# Revit family: PRD_FrankeWS_WtrSpplFttngsFrWshBsnsAndTrghs_PillarMixer_F5EM1001-1004,1007-1010
name_source: partatom
category: Plumbing Fixtures
revit_build: Autodesk Revit 2018 (Build: 20190510_1515(x64)
units: mm (PartAtom-declared; Revit-internal decimal feet)

## family parameters
Always vertical = Yes
Cut with Voids When Loaded = No
OmniClass Number = 23.45.55.14
OmniClass Title = Single Faucets
Part Type = Normal
Room Calculation Point = No
Round Connector Dimension = Use Diameter
Shared = No
Work Plane-Based = No

## types (8) — shared parameters
AssetType = Fixed
Category = Pr_40_20_87_98, Washbasin taps
Color = Chrome
DefaultAutomaticHygieneFlushing = 24H-AFTER-ACTIVITY
Depressurised = no
DurationUnit = year
FaucetFunction = MIXED
FaucetMaterial = PRD_AR_ChromatedBrass_HighPolished
FaucetOperation = SELFCLOSING
FaucetType = PILLAR
Finish = high-polished chromium-plated brass
FlowColdWater = 0.1 L/s
FlowHotWater = 0.1 L/s
Form = Self-closing
FunctionalPrinciple = ELECTRONIX-C
HygieneFlushing = yes
IfcExportAs = IfcValveType
IfcExportType = FAUCET
InletSize = G 3/8
Manufacturer = KWC Group AG
ManufacturerName = KWC Group AG
ManufacturerURL = www.kwc.com
Material = Brass
MaterialsBody = Brass
MaterialsFinishAndColour = high-polished chromium-plated brass
MinimumFlowPressure = 1.00 bar
NBSDescription = Water supply fittings for wash basins and troughs
NBSReference = 45-35-70/371
OutletMaterial = PRD_AR_SyntheticGrey
ProductInformation = https://pim.kwc.com
ProtectiveShutdown = yes
ProtectiveSystemIP = 59K
SensorMaterial = PRD_AR_SyntheticDarkGrey
SoundInsulation = no
SpoutProjection = 125.00 mm
ThermalDisinfection = no
TypeOfMixing = yes
TypeOfMounting = TAPHOLE
TypeOfOperation = SENSOR-OPERATION
TypeOfSensor = OPTO-ELEC-SENSOR
TypeOfTap = PILLAR-TAP
URL = www.kwc.com
Uniclass2015Code = Pr_40_20_87_98
Uniclass2015Title = Washbasin taps
Uniclass2015Version = Products v1.7
Version = 1
WarrantyDurationUnit = year
zero-valued in all types: NominalHeight, NominalLength, NominalWidth

## per-type parameters (varying)
| type | BIMObjectName | Description | FlowRateMaximum | GrossWeight | Model | ModelNumber | ModelReference | Name | NetWeight | NominalDiameter | PositionOfPowerConnection | PowerConsumption | PowerSupplyConnection |
| F5EM1001 - 0.08 L/s with 6 V lithium battery | PRD_AR_WaterSupplyFittingsForWashBasinsAndTroughs_ElectronicPillarMixer_F5EM1001 | F5E-Mix pillar mixer DN 15 for sanitary facilities, opto-electronically controlled. For connection to hot and cold water via hoses with integrated backflow preventer and strainers. Control electronics, solenoid valve cartridge, 6 V lithium battery (CR-P2) and sensor in all-metal housing, high-polished chromium-plated brass. Temperature lever with adjustable, turn-proof temperature stop as well as conversion set for concealed mixing device. Anti-theft aerator, design SLIM, with integrated flow regulator 5.0 l/min. Activated water hygiene flushing 24 hours after last activation, safety switch-off with continuous reflection and saving of statistical data. With option for parameterization and communication via optional, bidirectional remote control. | 0.08 L/s at 3 bar | 2.04 kg | F5EM1001 | 2030027923 | F5EM1001 | F5 pillar mixer F5EM1001 | 1.90 kg | 15 mm |  |  | Battery-6-V |
| F5EM1002 - 0.08 L/s with 100 - 240 V AC plug-in power supply unit | PRD_AR_WaterSupplyFittingsForWashBasinsAndTroughs_ElectronicPillarMixer_F5EM1002 | F5E-Mix pillar mixer DN 15 for sanitary facilities, opto-electronically controlled. For connection to hot and cold water via hoses with integrated backflow preventer and strainers. Control electronics, solenoid valve cartridge and sensor in all-metal housing, high-polished chromium-plated brass. Temperature lever with adjustable, turn-proof temperature stop as well as conversion set for concealed mixing device. Anti-theft aerator, design SLIM, with integrated flow regulator 5.0 l/min. Activated water hygiene flushing 24 hours after last activation, safety switch-off with continuous reflection and saving of statistical data. With option for parameterization and communication via optional, bidirectional remote control. With 100 - 240 V AC plug-in power supply unit. | 0.08 L/s at 3 bar | 1.90 kg | F5EM1002 | 2030035328 | F5EM1002 | F5 pillar mixer F5EM1002 | 1.82 kg | 15 mm | BOTTOM | 1.5 | 100-240VAC |
| F5EM1003 - 0.08 L/s with in-wall power supply 100 - 240 V AC | PRD_AR_WaterSupplyFittingsForWashBasinsAndTroughs_ElectronicPillarMixer_F5EM1003 | F5E-Mix pillar mixer DN 15 for sanitary facilities, opto-electronically controlled. For connection to hot and cold water via hoses with integrated backflow preventer and strainers. Control electronics, solenoid valve cartridge and sensor in all-metal housing, high-polished chromium-plated brass. Temperature lever with adjustable, turn-proof temperature stop as well as conversion set for concealed mixing device. Anti-theft aerator, design SLIM, with integrated flow regulator 5.0 l/min. Activated water hygiene flushing 24 hours after last activation, safety switch-off with continuous reflection and saving of statistical data. With option for parameterization and communication via optional, bidirectional remote control. With in-wall power supply 100 - 240 V AC. | 0.08 L/s at 3 bar | 1.90 kg | F5EM1003 | 2030035329 | F5EM1003 | F5 pillar mixer F5EM1003 | 1.81 kg | 15 mm | BOTTOM | 1.5 | 100-240VAC |
| F5EM1004 - 0.08 L/s with separate power supply via power supply unit 6.75 V / 12 V DC | PRD_AR_WaterSupplyFittingsForWashBasinsAndTroughs_ElectronicPillarMixer_F5EM1004 | F5E-Mix pillar mixer DN 15 for sanitary facilities, opto-electronically controlled. For connection to hot and cold water via hoses with integrated backflow preventer and strainers. Control electronics, solenoid valve cartridge and sensor in all-metal housing, high-polished chromium-plated brass. Temperature lever with adjustable, turn-proof temperature stop as well as conversion set for concealed mixing device. Anti-theft aerator, design SLIM, with integrated flow regulator 5.0 l/min. Activated water hygiene flushing 24 hours after last activation, safety switch-off with continuous reflection and saving of statistical data. With option for parameterization and communication via optional, bidirectional remote control. Separate power supply via power supply unit 6.75 V / 12 V DC or AQUA 3000 open system accessories. | 0.08 L/s at 3 bar | 3.94 kg | F5EM1004 | 2030036159 | F5EM1004 | F5 pillar mixer F5EM1004 | 3.80 kg | 0 mm | BOTTOM | 1.5 | 6 V DC, 12 V DC, A3000 open |
| F5EM1007 - 0.05 L/s with 6 V lithium battery | PRD_AR_WaterSupplyFittingsForWashBasinsAndTroughs_ElectronicPillarMixer_F5EM1007 | F5E-Mix pillar mixer DN 15 for sanitary facilities, opto-electronically controlled. For connection to hot and cold water via hoses with integrated backflow preventer and strainers. Control electronics, solenoid valve cartridge, 6 V lithium battery (CR-P2) and sensor in all-metal housing, high-polished chromium-plated brass. Temperature lever with adjustable, turn-proof temperature stop as well as conversion set for concealed mixing device. Aerator with integrated flow regulator 3.0 l/min. Activated water hygiene flushing 24 hours after last activation, safety switch-off with continuous reflection and saving of statistical data. With option for parameterization and communication via optional, bidirectional remote control. | 0.05 L/s at 3 bar | 1.90 kg | F5EM1007 | 2030039427 | F5EM1007 | F5 pillar mixer F5EM1007 | 1.81 kg | 15 mm |  |  | Battery-6-V |
| F5EM1008 - 0.05 L/s with 100 - 240 V AC plug-in power supply unit | PRD_AR_WaterSupplyFittingsForWashBasinsAndTroughs_ElectronicPillarMixer_F5EM1008 | F5E-Mix pillar mixer DN 15 for sanitary facilities, opto-electronically controlled. For connection to hot and cold water via hoses with integrated backflow preventer and strainers. Control electronics, solenoid valve cartridge and sensor in all-metal housing, high-polished chromium-plated brass. Temperature lever with adjustable, turn-proof temperature stop as well as conversion set for concealed mixing device. Aerator with integrated flow regulator 3.0 l/min. Activated water hygiene flushing 24 hours after last activation, safety switch-off with continuous reflection and saving of statistical data. With option for parameterization and communication via optional, bidirectional remote control. With 100 - 240 V AC plug-in power supply unit. | 0.05 L/s at 3 bar | 1.90 kg | F5EM1008 | 2030039431 | F5EM1008 | F5 pillar mixer F5EM1008 | 1.81 kg | 15 mm | BOTTOM | 1.5 | 100-240VAC |
| F5EM1009 - 0.05 L/s with in-wall power supply 100 - 240 V AC | PRD_AR_WaterSupplyFittingsForWashBasinsAndTroughs_ElectronicPillarMixer_F5EM1009 | F5E-Mix pillar mixer DN 15 for sanitary facilities, opto-electronically controlled. For connection to hot and cold water via hoses with integrated backflow preventer and strainers. Control electronics, solenoid valve cartridge and sensor in all-metal housing, high-polished chromium-plated brass. Temperature lever with adjustable, turn-proof temperature stop as well as conversion set for concealed mixing device. Aerator with integrated flow regulator 3.0 l/min. Activated water hygiene flushing 24 hours after last activation, safety switch-off with continuous reflection and saving of statistical data. With option for parameterization and communication via optional, bidirectional remote control. With in-wall power supply 100 - 240 V AC. | 0.05 L/s at 3 bar | 1.90 kg | F5EM1009 | 2030039432 | F5EM1009 | F5 pillar mixer F5EM1009 | 1.81 kg | 15 mm | BOTTOM | 1.5 | 100-240VAC |
| F5EM1010 - 0.05 L/s with separate power supply via power supply unit 6.75 V / 12 V DC | PRD_AR_WaterSupplyFittingsForWashBasinsAndTroughs_ElectronicPillarMixer_F5EM1010 | F5E-Mix pillar mixer DN 15 for sanitary facilities, opto-electronically controlled. For connection to hot and cold water via hoses with integrated backflow preventer and strainers. Control electronics, solenoid valve cartridge and sensor in all-metal housing, high-polished chromium-plated brass. Temperature lever with adjustable, turn-proof temperature stop as well as conversion set for concealed mixing device. Aerator with integrated flow regulator 3.0 l/min. Activated water hygiene flushing 24 hours after last activation, safety switch-off with continuous reflection and saving of statistical data. With option for parameterization and communication via optional, bidirectional remote control. Separate power supply via power supply unit 6.75 V / 12 V DC or AQUA 3000 open system accessories. | 0.05 L/s at 3 bar | 1.90 kg | F5EM1010 | 2030039434 | F5EM1010 | F5 pillar mixer F5EM1010 | 1.81 kg | 15 mm | BOTTOM | 1.5 | 6 V DC, 12 V DC, A3000 open |

## geometry (parser evidence)
native form markers: Sweep x2
no freeform markers — native parametric forms only
